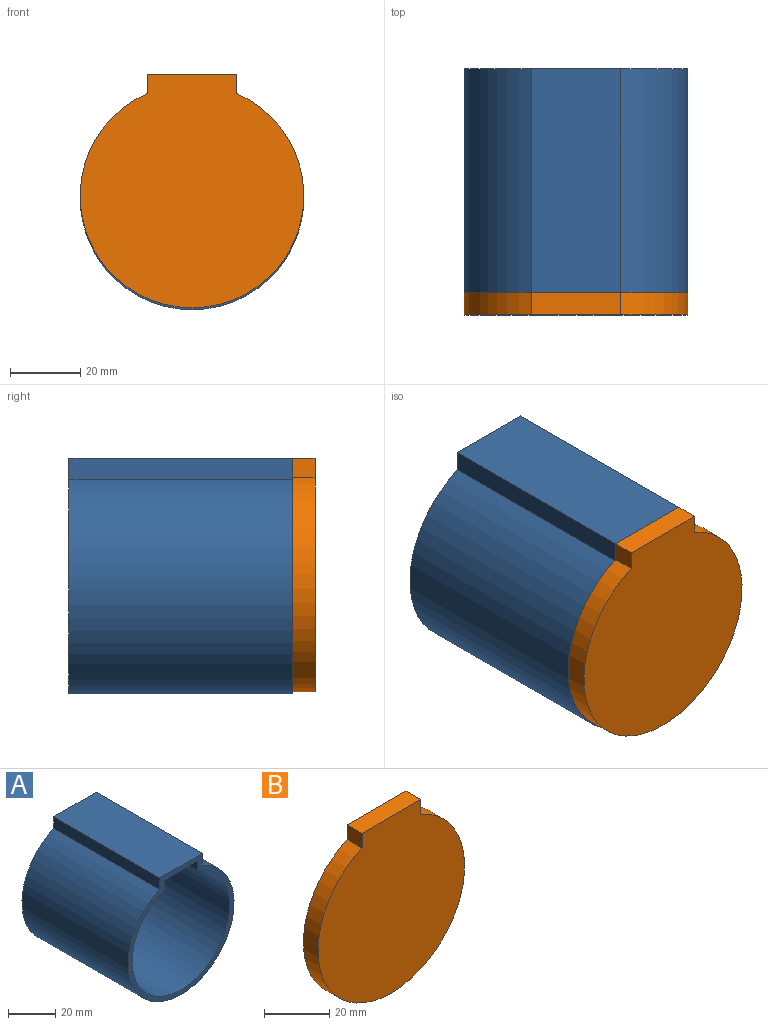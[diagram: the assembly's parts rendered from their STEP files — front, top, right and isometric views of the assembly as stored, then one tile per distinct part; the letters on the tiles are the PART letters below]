
ASSEMBLY  parts=2 mates=1
PART A: 11 faces, bbox 63.5x63.5x66.9 mm
  f0: plane 63.5x6.03mm, normal (-1,0,0), area 382.7mm2, adj f1,f3,f4,f5
  f1: cylinder r=31.75mm len=63.5mm, axis (0,1,0), area 11008.3mm2, adj f0,f2,f4,f5
  f2: plane 63.5x6.03mm, normal (1,0,0), area 382.7mm2, adj f1,f3,f4,f5
  f3: plane 63.5x25.4mm, normal (0,0,1), area 1612.9mm2, adj f0,f2,f4,f5
  f4: plane 66.88x63.5mm, normal (0,-1,0), area 513.4mm2, adj f0,f1,f2,f3,f6,f7,f8,f9
  f5: plane 66.88x63.5mm, normal (0,1,0), area 3274.7mm2, adj f0,f1,f2,f3
  f6: plane 60.96x5.2mm, normal (1,0,0), area 317mm2, adj f4,f7,f9,f10
  f7: cylinder r=29.21mm len=60.96mm, axis (0,1,0), area 9923mm2, adj f4,f6,f8,f10
  f8: plane 60.96x5.2mm, normal (-1,0,0), area 317mm2, adj f4,f7,f9,f10
  f9: plane 60.96x20.32mm, normal (0,0,-1), area 1238.7mm2, adj f4,f6,f8,f10
  f10: plane 61.8x58.42mm, normal (0,-1,0), area 2761.3mm2, adj f6,f7,f8,f9
PART B: 11 faces, bbox 63.5x6.4x66.3 mm
  f0: plane 6.35x5.46mm, normal (-1,0,0), area 34.6mm2, adj f1,f3,f4,f5
  f1: cylinder r=31.75mm len=63.5mm, axis (0,1,0), area 1100.8mm2, adj f0,f2,f4,f5
  f2: plane 6.35x5.46mm, normal (1,0,0), area 34.6mm2, adj f1,f3,f4,f5
  f3: plane 25.4x6.35mm, normal (0,0,1), area 161.3mm2, adj f0,f2,f4,f5
  f4: plane 66.3x63.5mm, normal (0,-1,0), area 3260.2mm2, adj f0,f1,f2,f3
  f5: plane 66.3x63.5mm, normal (0,1,0), area 510.5mm2, adj f0,f1,f2,f3,f6,f7,f8,f9
  f6: plane 4.63x3.81mm, normal (1,0,0), area 17.6mm2, adj f5,f7,f9,f10
  f7: cylinder r=29.21mm len=58.42mm, axis (0,1,0), area 620.2mm2, adj f5,f6,f8,f10
  f8: plane 4.63x3.81mm, normal (-1,0,0), area 17.6mm2, adj f5,f7,f9,f10
  f9: plane 20.32x3.81mm, normal (0,0,-1), area 77.4mm2, adj f5,f6,f8,f10
  f10: plane 61.22x58.42mm, normal (0,1,0), area 2749.7mm2, adj f6,f7,f8,f9
PLACE A t=(-33.38,0.18,-18.25)mm
PLACE B t=(-33.38,-63.32,-17.67)mm
MATE revolute B.f5 <-> A.f4  axis (0,1,0) through (-33.38,-63.32,16.88)mm
